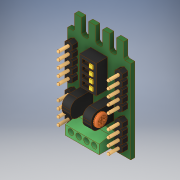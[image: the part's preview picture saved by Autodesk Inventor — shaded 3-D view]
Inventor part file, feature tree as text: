
AUTODESK INVENTOR PART (.ipt)
format: ipt  version: 2017 (Build 210142000, 142)  size: 359,936 bytes
history: native  units: in
note: dims shown in document units (in); Inventor stores cm internally (conversion verified against a paired STEP export)
features: mirror x1
ambient origin geometry x8: Origin, YZ Plane, XZ Plane, XY Plane, X Axis, Y Axis, Z Axis, Center Point
bodies: Solid1 (feature_tree)
feature tree (1):
  mirror  "Mirror3"
